# Revit family: 08. Wichmann Kabelbox SoniFoam_WAND
name_source: partatom
category: Mechanical Equipment
revit_build: Autodesk Revit 2018 (Build: 20170223_1515(x64)
units: mm (PartAtom-declared; Revit-internal decimal feet)

## family parameters
Always vertical = Yes
Cut with Voids When Loaded = No
Host = Wall
Part Type = Normal
Room Calculation Point = No
Round Connector Dimension = Use Diameter
Shared = No

## types (68) — shared parameters
Bautiefe = 270 mm
Höhe = 1725 mm
Rohbauöffnung = Yes

## per-type parameters (varying)
| type | Abst | Breite Außenmaß | Breite Innenmaß | Breite Rohbauöffnung | HAN | Höhe Außenmaß | Höhe Innenmaß | Höhe Rohbauöffnung | Höhe UK Durchbruch |
| Kabelbox SoniFoam, 110x435x270 mm | 75 mm  [stored 0.246063 ft] | 435 mm  [stored 1.42717 ft] | 405 mm | 475 mm  [stored 1.5584 ft] | SF110435 | 110 mm  [stored 0.360892 ft] | 70 mm  [stored 0.229659 ft] | 150 mm  [stored 0.492126 ft] | 1650 mm |
| Kabelbox SoniFoam, 110x380x270 mm | 75 mm  [stored 0.246063 ft] | 380 mm | 350 mm  [stored 1.14829 ft] | 420 mm  [stored 1.37795 ft] | SF110380 | 110 mm  [stored 0.360892 ft] | 70 mm  [stored 0.229659 ft] | 150 mm  [stored 0.492126 ft] | 1650 mm |
| Kabelbox SoniFoam, 110x335x270 mm | 75 mm  [stored 0.246063 ft] | 335 mm  [stored 1.09908 ft] | 305 mm  [stored 1.00066 ft] | 375 mm  [stored 1.23031 ft] | SF110335 | 110 mm  [stored 0.360892 ft] | 70 mm  [stored 0.229659 ft] | 150 mm  [stored 0.492126 ft] | 1650 mm |
| Kabelbox SoniFoam, 110x280x270 mm | 75 mm  [stored 0.246063 ft] | 280 mm  [stored 0.918635 ft] | 250 mm  [stored 0.82021 ft] | 320 mm  [stored 1.04987 ft] | SF110280 | 110 mm  [stored 0.360892 ft] | 70 mm  [stored 0.229659 ft] | 150 mm  [stored 0.492126 ft] | 1650 mm |
| Kabelbox SoniFoam, 110x200x270 mm | 75 mm  [stored 0.246063 ft] | 200 mm  [stored 0.656168 ft] | 170 mm  [stored 0.557743 ft] | 240 mm  [stored 0.787402 ft] | SF110200 | 110 mm  [stored 0.360892 ft] | 70 mm  [stored 0.229659 ft] | 150 mm  [stored 0.492126 ft] | 1650 mm |
| Kabelbox SoniFoam, 110x180x270 mm | 75 mm  [stored 0.246063 ft] | 180 mm  [stored 0.590551 ft] | 150 mm  [stored 0.492126 ft] | 220 mm  [stored 0.721785 ft] | SF110180 | 110 mm  [stored 0.360892 ft] | 70 mm  [stored 0.229659 ft] | 150 mm  [stored 0.492126 ft] | 1650 mm |
| Kabelbox SoniFoam, 110x160x270 mm | 75 mm  [stored 0.246063 ft] | 160 mm  [stored 0.524934 ft] | 130 mm  [stored 0.426509 ft] | 200 mm  [stored 0.656168 ft] | SF110160 | 110 mm  [stored 0.360892 ft] | 70 mm  [stored 0.229659 ft] | 150 mm  [stored 0.492126 ft] | 1650 mm |
| Kabelbox SoniFoam, 110x120x270 mm | 75 mm  [stored 0.246063 ft] | 120 mm  [stored 0.393701 ft] | 90 mm  [stored 0.295276 ft] | 160 mm  [stored 0.524934 ft] | SF110120 | 110 mm  [stored 0.360892 ft] | 70 mm  [stored 0.229659 ft] | 150 mm  [stored 0.492126 ft] | 1650 mm |
| Kabelbox SoniFoam, 100x640x270 mm | 70 mm  [stored 0.229659 ft] | 640 mm | 610 mm | 680 mm | SF100640 | 100 mm  [stored 0.328084 ft] | 64 mm  [stored 0.209974 ft] | 140 mm  [stored 0.459318 ft] | 1655 mm |
| Kabelbox SoniFoam, 100x580x270 mm | 70 mm  [stored 0.229659 ft] | 580 mm | 550 mm | 620 mm | SF100580 | 100 mm  [stored 0.328084 ft] | 64 mm  [stored 0.209974 ft] | 140 mm  [stored 0.459318 ft] | 1655 mm |
| Kabelbox SoniFoam, 100x535x270 mm | 70 mm  [stored 0.229659 ft] | 535 mm | 505 mm  [stored 1.65682 ft] | 575 mm | SF100535 | 100 mm  [stored 0.328084 ft] | 64 mm  [stored 0.209974 ft] | 140 mm  [stored 0.459318 ft] | 1655 mm |
| Kabelbox SoniFoam, 100x480x270 mm | 70 mm  [stored 0.229659 ft] | 480 mm  [stored 1.5748 ft] | 450 mm  [stored 1.47638 ft] | 520 mm  [stored 1.70604 ft] | SF100480 | 100 mm  [stored 0.328084 ft] | 64 mm  [stored 0.209974 ft] | 140 mm  [stored 0.459318 ft] | 1655 mm |
| Kabelbox SoniFoam, 100x435x270 mm | 70 mm  [stored 0.229659 ft] | 435 mm  [stored 1.42717 ft] | 405 mm | 475 mm  [stored 1.5584 ft] | SF100435 | 100 mm  [stored 0.328084 ft] | 64 mm  [stored 0.209974 ft] | 140 mm  [stored 0.459318 ft] | 1655 mm |
| Kabelbox SoniFoam, 100x380x270 mm | 70 mm  [stored 0.229659 ft] | 380 mm | 350 mm  [stored 1.14829 ft] | 420 mm  [stored 1.37795 ft] | SF100380 | 100 mm  [stored 0.328084 ft] | 64 mm  [stored 0.209974 ft] | 140 mm  [stored 0.459318 ft] | 1655 mm |
| Kabelbox SoniFoam, 100x280x270 mm | 70 mm  [stored 0.229659 ft] | 280 mm  [stored 0.918635 ft] | 250 mm  [stored 0.82021 ft] | 320 mm  [stored 1.04987 ft] | SF100280 | 100 mm  [stored 0.328084 ft] | 64 mm  [stored 0.209974 ft] | 140 mm  [stored 0.459318 ft] | 1655 mm |
| Kabelbox SoniFoam, 100x240x270 mm | 70 mm  [stored 0.229659 ft] | 240 mm  [stored 0.787402 ft] | 210 mm  [stored 0.688976 ft] | 280 mm  [stored 0.918635 ft] | SF100240 | 100 mm  [stored 0.328084 ft] | 64 mm  [stored 0.209974 ft] | 140 mm  [stored 0.459318 ft] | 1655 mm |
| Kabelbox SoniFoam, 100x200x270 mm | 70 mm  [stored 0.229659 ft] | 200 mm  [stored 0.656168 ft] | 170 mm  [stored 0.557743 ft] | 240 mm  [stored 0.787402 ft] | SF100200 | 100 mm  [stored 0.328084 ft] | 64 mm  [stored 0.209974 ft] | 140 mm  [stored 0.459318 ft] | 1655 mm |
| Kabelbox SoniFoam, 100x180x270 mm | 70 mm  [stored 0.229659 ft] | 180 mm  [stored 0.590551 ft] | 150 mm  [stored 0.492126 ft] | 220 mm  [stored 0.721785 ft] | SF100180 | 100 mm  [stored 0.328084 ft] | 64 mm  [stored 0.209974 ft] | 140 mm  [stored 0.459318 ft] | 1655 mm |
| Kabelbox SoniFoam, 100x160x270 mm | 70 mm  [stored 0.229659 ft] | 160 mm  [stored 0.524934 ft] | 130 mm  [stored 0.426509 ft] | 200 mm  [stored 0.656168 ft] | SF100160 | 100 mm  [stored 0.328084 ft] | 64 mm  [stored 0.209974 ft] | 140 mm  [stored 0.459318 ft] | 1655 mm |
| Kabelbox SoniFoam, 100x120x270 mm | 70 mm  [stored 0.229659 ft] | 120 mm  [stored 0.393701 ft] | 90 mm  [stored 0.295276 ft] | 160 mm  [stored 0.524934 ft] | SF100120 | 100 mm  [stored 0.328084 ft] | 64 mm  [stored 0.209974 ft] | 140 mm  [stored 0.459318 ft] | 1655 mm |
| Kabelbox SoniFoam, 90x640x270 mm | 65 mm  [stored 0.213255 ft] | 640 mm | 610 mm | 680 mm | SF090640 | 90 mm  [stored 0.295276 ft] | 56 mm  [stored 0.183727 ft] | 130 mm  [stored 0.426509 ft] | 1660 mm |
| Kabelbox SoniFoam, 90x580x270 mm | 65 mm  [stored 0.213255 ft] | 580 mm | 550 mm | 620 mm | SF090580 | 90 mm  [stored 0.295276 ft] | 56 mm  [stored 0.183727 ft] | 130 mm  [stored 0.426509 ft] | 1660 mm |
| Kabelbox SoniFoam, 90x535x270 mm | 65 mm  [stored 0.213255 ft] | 535 mm | 505 mm  [stored 1.65682 ft] | 575 mm | SF090535 | 90 mm  [stored 0.295276 ft] | 56 mm  [stored 0.183727 ft] | 130 mm  [stored 0.426509 ft] | 1660 mm |
| Kabelbox SoniFoam, 90x480x270 mm | 65 mm  [stored 0.213255 ft] | 480 mm  [stored 1.5748 ft] | 450 mm  [stored 1.47638 ft] | 520 mm  [stored 1.70604 ft] | SF090480 | 90 mm  [stored 0.295276 ft] | 56 mm  [stored 0.183727 ft] | 130 mm  [stored 0.426509 ft] | 1660 mm |
| Kabelbox SoniFoam, 90x380x270 mm | 65 mm  [stored 0.213255 ft] | 380 mm | 350 mm  [stored 1.14829 ft] | 420 mm  [stored 1.37795 ft] | SF090380 | 90 mm  [stored 0.295276 ft] | 56 mm  [stored 0.183727 ft] | 130 mm  [stored 0.426509 ft] | 1660 mm |
| Kabelbox SoniFoam, 60x180x270 mm | 50 mm  [stored 0.164042 ft] | 180 mm  [stored 0.590551 ft] | 150 mm  [stored 0.492126 ft] | 220 mm  [stored 0.721785 ft] | SF060180 | 60 mm  [stored 0.19685 ft] | 33 mm  [stored 0.108268 ft] | 100 mm  [stored 0.328084 ft] | 1675 mm |
| Kabelbox SoniFoam, 60x240x270 mm | 50 mm  [stored 0.164042 ft] | 240 mm  [stored 0.787402 ft] | 210 mm  [stored 0.688976 ft] | 280 mm  [stored 0.918635 ft] | SF060240 | 60 mm  [stored 0.19685 ft] | 33 mm  [stored 0.108268 ft] | 100 mm  [stored 0.328084 ft] | 1675 mm |
| Kabelbox SoniFoam, 60x280x270 mm | 50 mm  [stored 0.164042 ft] | 280 mm  [stored 0.918635 ft] | 250 mm  [stored 0.82021 ft] | 320 mm  [stored 1.04987 ft] | SF060280 | 60 mm  [stored 0.19685 ft] | 33 mm  [stored 0.108268 ft] | 100 mm  [stored 0.328084 ft] | 1675 mm |
| Kabelbox SoniFoam, 60x335x270 mm | 50 mm  [stored 0.164042 ft] | 335 mm  [stored 1.09908 ft] | 305 mm  [stored 1.00066 ft] | 375 mm  [stored 1.23031 ft] | SF060335 | 60 mm  [stored 0.19685 ft] | 33 mm  [stored 0.108268 ft] | 100 mm  [stored 0.328084 ft] | 1675 mm |
| Kabelbox SoniFoam, 60x435x270 mm | 50 mm  [stored 0.164042 ft] | 435 mm  [stored 1.42717 ft] | 405 mm | 475 mm  [stored 1.5584 ft] | SF060435 | 60 mm  [stored 0.19685 ft] | 33 mm  [stored 0.108268 ft] | 100 mm  [stored 0.328084 ft] | 1675 mm |
| Kabelbox SoniFoam, 60x480x270 mm | 50 mm  [stored 0.164042 ft] | 480 mm  [stored 1.5748 ft] | 450 mm  [stored 1.47638 ft] | 520 mm  [stored 1.70604 ft] | SF060480 | 60 mm  [stored 0.19685 ft] | 33 mm  [stored 0.108268 ft] | 100 mm  [stored 0.328084 ft] | 1675 mm |
| Kabelbox SoniFoam, 60x535x270 mm | 50 mm  [stored 0.164042 ft] | 535 mm | 505 mm  [stored 1.65682 ft] | 575 mm | SF060535 | 60 mm  [stored 0.19685 ft] | 33 mm  [stored 0.108268 ft] | 100 mm  [stored 0.328084 ft] | 1675 mm |
| Kabelbox SoniFoam, 80x180x270 mm | 60 mm  [stored 0.19685 ft] | 180 mm  [stored 0.590551 ft] | 150 mm  [stored 0.492126 ft] | 220 mm  [stored 0.721785 ft] | SF080180 | 80 mm  [stored 0.262467 ft] | 50 mm  [stored 0.164042 ft] | 120 mm  [stored 0.393701 ft] | 1665 mm |
| Kabelbox SoniFoam, 60x380x270 mm | 50 mm  [stored 0.164042 ft] | 380 mm | 350 mm  [stored 1.14829 ft] | 420 mm  [stored 1.37795 ft] | SF060380 | 60 mm  [stored 0.19685 ft] | 33 mm  [stored 0.108268 ft] | 100 mm  [stored 0.328084 ft] | 1675 mm |
| Kabelbox SoniFoam, 60x640x270 mm | 50 mm  [stored 0.164042 ft] | 640 mm | 610 mm | 680 mm | SF060640 | 60 mm  [stored 0.19685 ft] | 33 mm  [stored 0.108268 ft] | 100 mm  [stored 0.328084 ft] | 1675 mm |
| Kabelbox SoniFoam, 60x580x270 mm | 50 mm  [stored 0.164042 ft] | 580 mm | 550 mm | 620 mm | SF060580 | 60 mm  [stored 0.19685 ft] | 33 mm  [stored 0.108268 ft] | 100 mm  [stored 0.328084 ft] | 1675 mm |
| Kabelbox SoniFoam, 110x640x270 mm | 75 mm  [stored 0.246063 ft] | 640 mm | 610 mm | 680 mm | SF110640 | 110 mm  [stored 0.360892 ft] | 70 mm  [stored 0.229659 ft] | 150 mm  [stored 0.492126 ft] | 1650 mm |
| Kabelbox SoniFoam, 80x160x270 mm | 60 mm  [stored 0.19685 ft] | 160 mm  [stored 0.524934 ft] | 130 mm  [stored 0.426509 ft] | 200 mm  [stored 0.656168 ft] | SF080160 | 80 mm  [stored 0.262467 ft] | 50 mm  [stored 0.164042 ft] | 120 mm  [stored 0.393701 ft] | 1665 mm |
| Kabelbox SoniFoam, 80x90x270 mm | 60 mm  [stored 0.19685 ft] | 90 mm  [stored 0.295276 ft] | 60 mm  [stored 0.19685 ft] | 130 mm  [stored 0.426509 ft] | SF080090 | 80 mm  [stored 0.262467 ft] | 50 mm  [stored 0.164042 ft] | 120 mm  [stored 0.393701 ft] | 1665 mm |
| Kabelbox SoniFoam, 80x280x270 mm | 60 mm  [stored 0.19685 ft] | 280 mm  [stored 0.918635 ft] | 250 mm  [stored 0.82021 ft] | 320 mm  [stored 1.04987 ft] | SF080280 | 80 mm  [stored 0.262467 ft] | 50 mm  [stored 0.164042 ft] | 120 mm  [stored 0.393701 ft] | 1665 mm |
| Kabelbox SoniFoam, 80x335x270 mm | 60 mm  [stored 0.19685 ft] | 335 mm  [stored 1.09908 ft] | 305 mm  [stored 1.00066 ft] | 375 mm  [stored 1.23031 ft] | SF080335 | 80 mm  [stored 0.262467 ft] | 50 mm  [stored 0.164042 ft] | 120 mm  [stored 0.393701 ft] | 1665 mm |
| Kabelbox SoniFoam, 80x380x270 mm | 60 mm  [stored 0.19685 ft] | 380 mm | 350 mm  [stored 1.14829 ft] | 420 mm  [stored 1.37795 ft] | SF080380 | 80 mm  [stored 0.262467 ft] | 50 mm  [stored 0.164042 ft] | 120 mm  [stored 0.393701 ft] | 1665 mm |
| Kabelbox SoniFoam, 80x200x270 mm | 60 mm  [stored 0.19685 ft] | 200 mm  [stored 0.656168 ft] | 170 mm  [stored 0.557743 ft] | 240 mm  [stored 0.787402 ft] | SF080200 | 80 mm  [stored 0.262467 ft] | 50 mm  [stored 0.164042 ft] | 120 mm  [stored 0.393701 ft] | 1665 mm |
| Kabelbox SoniFoam, 80x240x270 mm | 60 mm  [stored 0.19685 ft] | 240 mm  [stored 0.787402 ft] | 210 mm  [stored 0.688976 ft] | 280 mm  [stored 0.918635 ft] | SF080240 | 80 mm  [stored 0.262467 ft] | 50 mm  [stored 0.164042 ft] | 120 mm  [stored 0.393701 ft] | 1665 mm |
| Kabelbox SoniFoam, 80x480x270 mm | 60 mm  [stored 0.19685 ft] | 480 mm  [stored 1.5748 ft] | 450 mm  [stored 1.47638 ft] | 520 mm  [stored 1.70604 ft] | SF080480 | 80 mm  [stored 0.262467 ft] | 50 mm  [stored 0.164042 ft] | 120 mm  [stored 0.393701 ft] | 1665 mm |
| Kabelbox SoniFoam, 80x435x270 mm | 60 mm  [stored 0.19685 ft] | 435 mm  [stored 1.42717 ft] | 405 mm | 475 mm  [stored 1.5584 ft] | SF080435 | 80 mm  [stored 0.262467 ft] | 50 mm  [stored 0.164042 ft] | 120 mm  [stored 0.393701 ft] | 1665 mm |
| Kabelbox SoniFoam, 90x90x270 mm | 65 mm  [stored 0.213255 ft] | 90 mm  [stored 0.295276 ft] | 60 mm  [stored 0.19685 ft] | 130 mm  [stored 0.426509 ft] | SF090090 | 90 mm  [stored 0.295276 ft] | 56 mm  [stored 0.183727 ft] | 130 mm  [stored 0.426509 ft] | 1660 mm |
| Kabelbox SoniFoam, 80x640x270 mm | 60 mm  [stored 0.19685 ft] | 640 mm | 610 mm | 680 mm | SF080640 | 80 mm  [stored 0.262467 ft] | 50 mm  [stored 0.164042 ft] | 120 mm  [stored 0.393701 ft] | 1665 mm |
| Kabelbox SoniFoam, 80x535x270 mm | 60 mm  [stored 0.19685 ft] | 535 mm | 505 mm  [stored 1.65682 ft] | 575 mm | SF080535 | 80 mm  [stored 0.262467 ft] | 50 mm  [stored 0.164042 ft] | 120 mm  [stored 0.393701 ft] | 1665 mm |
| Kabelbox SoniFoam, 90x180x270 mm | 65 mm  [stored 0.213255 ft] | 180 mm  [stored 0.590551 ft] | 150 mm  [stored 0.492126 ft] | 220 mm  [stored 0.721785 ft] | SF090180 | 90 mm  [stored 0.295276 ft] | 56 mm  [stored 0.183727 ft] | 130 mm  [stored 0.426509 ft] | 1660 mm |
| Kabelbox SoniFoam, 90x200x270 mm | 65 mm  [stored 0.213255 ft] | 200 mm  [stored 0.656168 ft] | 170 mm  [stored 0.557743 ft] | 240 mm  [stored 0.787402 ft] | SF090200 | 90 mm  [stored 0.295276 ft] | 56 mm  [stored 0.183727 ft] | 130 mm  [stored 0.426509 ft] | 1660 mm |
| Kabelbox SoniFoam, 90x240x270 mm | 65 mm  [stored 0.213255 ft] | 240 mm  [stored 0.787402 ft] | 210 mm  [stored 0.688976 ft] | 280 mm  [stored 0.918635 ft] | SF090240 | 90 mm  [stored 0.295276 ft] | 56 mm  [stored 0.183727 ft] | 130 mm  [stored 0.426509 ft] | 1660 mm |
| Kabelbox SoniFoam, 90x120x270 mm | 65 mm  [stored 0.213255 ft] | 120 mm  [stored 0.393701 ft] | 90 mm  [stored 0.295276 ft] | 160 mm  [stored 0.524934 ft] | SF090120 | 90 mm  [stored 0.295276 ft] | 56 mm  [stored 0.183727 ft] | 130 mm  [stored 0.426509 ft] | 1660 mm |
| Kabelbox SoniFoam, 90x160x270 mm | 65 mm  [stored 0.213255 ft] | 160 mm  [stored 0.524934 ft] | 130 mm  [stored 0.426509 ft] | 200 mm  [stored 0.656168 ft] | SF090160 | 90 mm  [stored 0.295276 ft] | 56 mm  [stored 0.183727 ft] | 130 mm  [stored 0.426509 ft] | 1660 mm |
| Kabelbox SoniFoam, 90x335x270 mm | 65 mm  [stored 0.213255 ft] | 335 mm  [stored 1.09908 ft] | 305 mm  [stored 1.00066 ft] | 375 mm  [stored 1.23031 ft] | SF090335 | 90 mm  [stored 0.295276 ft] | 56 mm  [stored 0.183727 ft] | 130 mm  [stored 0.426509 ft] | 1660 mm |
| Kabelbox SoniFoam, 90x280x270 mm | 65 mm  [stored 0.213255 ft] | 280 mm  [stored 0.918635 ft] | 250 mm  [stored 0.82021 ft] | 320 mm  [stored 1.04987 ft] | SF090280 | 90 mm  [stored 0.295276 ft] | 56 mm  [stored 0.183727 ft] | 130 mm  [stored 0.426509 ft] | 1660 mm |
| Kabelbox SoniFoam, 80x580x270 mm | 60 mm  [stored 0.19685 ft] | 580 mm | 550 mm | 620 mm | SF080580 | 80 mm  [stored 0.262467 ft] | 50 mm  [stored 0.164042 ft] | 120 mm  [stored 0.393701 ft] | 1665 mm |
| Kabelbox SoniFoam, 80x120x270 mm | 60 mm  [stored 0.19685 ft] | 120 mm  [stored 0.393701 ft] | 90 mm  [stored 0.295276 ft] | 160 mm  [stored 0.524934 ft] | SF080120 | 80 mm  [stored 0.262467 ft] | 50 mm  [stored 0.164042 ft] | 120 mm  [stored 0.393701 ft] | 1665 mm |
| Kabelbox SoniFoam, 60x200x270 mm | 50 mm  [stored 0.164042 ft] | 200 mm  [stored 0.656168 ft] | 170 mm  [stored 0.557743 ft] | 240 mm  [stored 0.787402 ft] | SF060200 | 60 mm  [stored 0.19685 ft] | 33 mm  [stored 0.108268 ft] | 100 mm  [stored 0.328084 ft] | 1675 mm |
| Kabelbox SoniFoam, 110x240x270 mm | 75 mm  [stored 0.246063 ft] | 240 mm  [stored 0.787402 ft] | 210 mm  [stored 0.688976 ft] | 280 mm  [stored 0.918635 ft] | SF110240 | 110 mm  [stored 0.360892 ft] | 70 mm  [stored 0.229659 ft] | 150 mm  [stored 0.492126 ft] | 1650 mm |
| Kabelbox SoniFoam, 110x480x270 mm | 75 mm  [stored 0.246063 ft] | 480 mm  [stored 1.5748 ft] | 450 mm  [stored 1.47638 ft] | 520 mm  [stored 1.70604 ft] | SF110480 | 110 mm  [stored 0.360892 ft] | 70 mm  [stored 0.229659 ft] | 150 mm  [stored 0.492126 ft] | 1650 mm |
| Kabelbox SoniFoam, 110x535x270 mm | 75 mm  [stored 0.246063 ft] | 535 mm | 505 mm  [stored 1.65682 ft] | 575 mm | SF110535 | 110 mm  [stored 0.360892 ft] | 70 mm  [stored 0.229659 ft] | 150 mm  [stored 0.492126 ft] | 1650 mm |
| Kabelbox SoniFoam, 90x435x270 mm | 65 mm  [stored 0.213255 ft] | 435 mm  [stored 1.42717 ft] | 405 mm | 475 mm  [stored 1.5584 ft] | SF090435 | 90 mm  [stored 0.295276 ft] | 56 mm  [stored 0.183727 ft] | 130 mm  [stored 0.426509 ft] | 1660 mm |
| Kabelbox SoniFoam, 100x335x270 mm | 70 mm  [stored 0.229659 ft] | 335 mm  [stored 1.09908 ft] | 305 mm  [stored 1.00066 ft] | 375 mm  [stored 1.23031 ft] | SF100335 | 100 mm  [stored 0.328084 ft] | 64 mm  [stored 0.209974 ft] | 140 mm  [stored 0.459318 ft] | 1655 mm |
| Kabelbox SoniFoam, 60x90x270 mm | 50 mm  [stored 0.164042 ft] | 90 mm  [stored 0.295276 ft] | 60 mm  [stored 0.19685 ft] | 130 mm  [stored 0.426509 ft] | SF060090 | 60 mm  [stored 0.19685 ft] | 33 mm  [stored 0.108268 ft] | 100 mm  [stored 0.328084 ft] | 1675 mm |
| Kabelbox SoniFoam, 110x580x270 mm | 75 mm  [stored 0.246063 ft] | 580 mm | 550 mm | 620 mm | SF110580 | 110 mm  [stored 0.360892 ft] | 70 mm  [stored 0.229659 ft] | 150 mm  [stored 0.492126 ft] | 1650 mm |
| Kabelbox SoniFoam, 60x160x270 mm | 50 mm  [stored 0.164042 ft] | 160 mm  [stored 0.524934 ft] | 130 mm  [stored 0.426509 ft] | 200 mm  [stored 0.656168 ft] | SF060160 | 60 mm  [stored 0.19685 ft] | 33 mm  [stored 0.108268 ft] | 100 mm  [stored 0.328084 ft] | 1675 mm |
| Kabelbox SoniFoam, 60x120x270 mm | 50 mm  [stored 0.164042 ft] | 120 mm  [stored 0.393701 ft] | 90 mm  [stored 0.295276 ft] | 160 mm  [stored 0.524934 ft] | SF060120 | 60 mm  [stored 0.19685 ft] | 33 mm  [stored 0.108268 ft] | 100 mm  [stored 0.328084 ft] | 1675 mm |

note: [stored X ft] marks values corroborated as IEEE doubles in the binary element streams (Revit-internal decimal feet)
